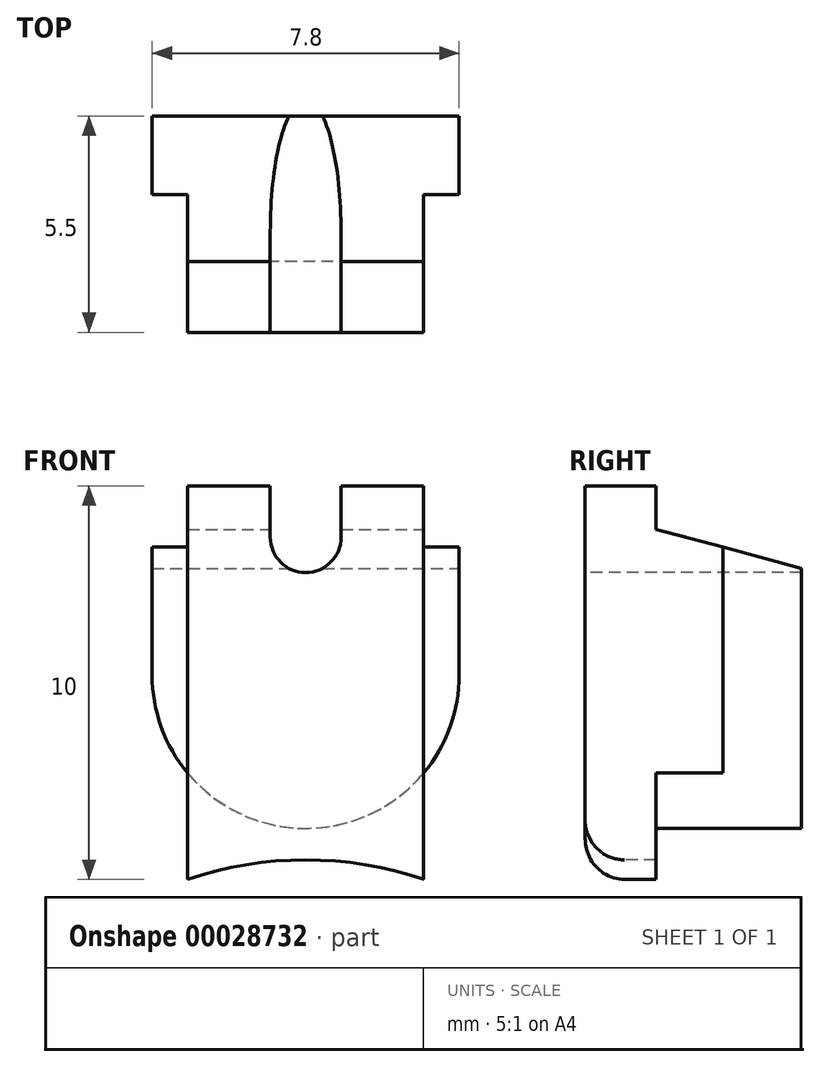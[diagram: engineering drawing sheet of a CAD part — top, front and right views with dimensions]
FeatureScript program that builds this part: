
annotation { "Feature Type Name" : "Feature", "Feature Type Description" : "" }
export const myFeature = defineFeature(function(context is Context, id is Id, definition is map)
    precondition{}
    {
        {
            var Q0;
            Q0=qCreatedBy(makeId("Front.planeOp"),FACE);
            var sketch = newSketch(context, id + "F0", { "sketchPlane" : qUnion([Q0])});
            skLineSegment(sketch, "E0", {"start": v(0, 8.83) * mm, "end": v(0, -12.43) * mm, "construction": true});
            skLineSegment(sketch, "E1.bottom", {"start": v(-3.9, 0) * mm, "end": v(0, 0) * mm});
            skLineSegment(sketch, "E1.top", {"start": v(-3.9, -10) * mm, "end": v(-3, -10) * mm});
            skLineSegment(sketch, "E1.left", {"start": v(-3.9, 0) * mm, "end": v(-3.9, -10) * mm});
            skLineSegment(sketch, "E1.right", {"start": v(3.9, 0) * mm, "end": v(3.9, -10) * mm});
            skLineSegment(sketch, "E2", {"start": v(-3, 0) * mm, "end": v(-3, -10) * mm});
            skLineSegment(sketch, "E3", {"start": v(3, 0) * mm, "end": v(3, -10) * mm});
            skLineSegment(sketch, "E4", {"start": v(-5.66, -9.5) * mm, "end": v(6.1, -9.5) * mm, "construction": true});
            skLineSegment(sketch, "E5", {"start": v(-5.46, -8.7) * mm, "end": v(6.54, -8.7) * mm, "construction": true});
            skLineSegment(sketch, "E6", {"start": v(-0.9, 0) * mm, "end": v(-0.9, -1.3) * mm});
            skArc(sketch, "E7", {"start": v(-0.9, -1.3) * mm, "mid": v(0, -2.2) * mm, "end": v(0.9, -1.3) * mm});
            skLineSegment(sketch, "E8", {"start": v(0.9, -1.3) * mm, "end": v(0.9, 0) * mm});
            skLineSegment(sketch, "E9.trimOffspring", {"start": v(0.9, 0) * mm, "end": v(3.9, 0) * mm});
            skArc(sketch, "E10", {"start": v(3, -10) * mm, "mid": v(0, -9.5) * mm, "end": v(-3, -10) * mm});
            skLineSegment(sketch, "E11.trimOffspring", {"start": v(3, -10) * mm, "end": v(3.9, -10) * mm});
            skArc(sketch, "E12", {"start": v(-3.9, -4.8) * mm, "mid": v(0, -8.7) * mm, "end": v(3.9, -4.8) * mm});
            skSolve(sketch);
        }
        {
            var Q0;
            Q0 = qSketchRegion(id + "F0", true);
            extrude(context, id + "F1", {"entities" : qUnion([Q0]), "oppositeDirection" : true, "depth" : 5.5 * mm});
        }
        {
            var Q0;
            Q0=makeQuery(id+"F1.opExtrude","SWEPT_FACE",FACE,{"disambiguationData":[OSD([sQuery(id+"F0.wireOp",EDGE,"E1.right")])]});
            var sketch = newSketch(context, id + "F2", { "sketchPlane" : qUnion([Q0])});
            skLineSegment(sketch, "E13", {"start": v(1.8, 0) * mm, "end": v(1.8, -1.1) * mm});
            skLineSegment(sketch, "E14", {"start": v(1.8, -1.1) * mm, "end": v(5.5, -2.1) * mm});
            skLineSegment(sketch, "E15", {"start": v(5.5, -2.1) * mm, "end": v(5.5, 0) * mm});
            skLineSegment(sketch, "E16", {"start": v(5.5, 0) * mm, "end": v(1.8, 0) * mm});
            skLineSegment(sketch, "E17", {"start": v(5.5, -8.7) * mm, "end": v(1.8, -8.7) * mm});
            skLineSegment(sketch, "E18", {"start": v(1.8, -8.7) * mm, "end": v(1.8, -10) * mm});
            skLineSegment(sketch, "E19", {"start": v(1.8, -10) * mm, "end": v(5.5, -10) * mm});
            skLineSegment(sketch, "E20", {"start": v(5.5, -10) * mm, "end": v(5.5, -8.7) * mm});
            skLineSegment(sketch, "E21", {"start": v(3.5, -1.56) * mm, "end": v(3.5, -8.7) * mm, "construction": true});
            skSolve(sketch);
        }
        {
            var Q0;
            Q0 = qSketchRegion(id + "F2", true);
            extrude(context, id + "F3", {"entities" : qUnion([Q0]), "operationType" : NewBodyOperationType.REMOVE, "endBound" : BoundingType.THROUGH_ALL, "oppositeDirection" : true, "depth" : 25 * mm});
        }
        {
            var Q0;
            Q0=sQuery(id+"F2.wireOp",VERTEX,"E21.end");
            var Q1;
            Q1=qCreatedBy(makeId("Front.planeOp"),FACE);
            cPlane(context, id + "F4", {"entities" : qUnion([Q0, Q1]), "cplaneType" : CPlaneType.PLANE_POINT, "offset" : 150 * mm, "width" : 150 * mm, "height" : 150 * mm});
        }
        {
            var Q0;
            Q0=qCreatedBy(id+"F4.planeOp",FACE);
            var sketch = newSketch(context, id + "F5", { "sketchPlane" : qUnion([Q0])});
            skLineSegment(sketch, "E22.0", {"start": v(3, 0) * mm, "end": v(3, -10) * mm});
            skLineSegment(sketch, "E22.1", {"start": v(-3, 0) * mm, "end": v(-3, -10) * mm});
            skLineSegment(sketch, "E23", {"start": v(3, 0) * mm, "end": v(3.9, 0) * mm});
            skLineSegment(sketch, "E24", {"start": v(3.9, 0) * mm, "end": v(3.9, -10) * mm});
            skLineSegment(sketch, "E25", {"start": v(3.9, -10) * mm, "end": v(3, -10) * mm});
            skLineSegment(sketch, "E26", {"start": v(-3, 0) * mm, "end": v(-3.9, 0) * mm});
            skLineSegment(sketch, "E27", {"start": v(-3.9, 0) * mm, "end": v(-3.9, -10) * mm});
            skLineSegment(sketch, "E28", {"start": v(-3.9, -10) * mm, "end": v(-3, -10) * mm});
            skSolve(sketch);
        }
        {
            var Q0;
            Q0 = qSketchRegion(id + "F5", true);
            extrude(context, id + "F6", {"entities" : qUnion([Q0]), "operationType" : NewBodyOperationType.REMOVE, "endBound" : BoundingType.THROUGH_ALL, "depth" : 25 * mm});
        }
        {
            var Q0;
            Q0=makeQuery(id+"F1.opExtrude","CAP_EDGE",EDGE,{"disambiguationData":[OSD([sQuery(id+"F0.wireOp",EDGE,"E10")])],"isStart":true});
            fillet(context, id + "F7", {"entities" : qUnion([Q0]), "radius" : 1 * mm, "tangentPropagation" : true, "allowEdgeOverflow" : false});
        }
        {
            var Q0;
            Q0=makeQuery(id+"F1.opExtrude","CAP_FACE",FACE,{"disambiguationData":[OSD([sQuery(id+"F0.wireOp",EDGE,"E1.bottom"),sQuery(id+"F0.wireOp",EDGE,"E1.top"),sQuery(id+"F0.wireOp",EDGE,"E1.left"),sQuery(id+"F0.wireOp",EDGE,"E1.right"),sQuery(id+"F0.wireOp",EDGE,"E6"),sQuery(id+"F0.wireOp",EDGE,"E7"),sQuery(id+"F0.wireOp",EDGE,"E8"),sQuery(id+"F0.wireOp",EDGE,"E9.trimOffspring"),sQuery(id+"F0.wireOp",EDGE,"E10"),sQuery(id+"F0.wireOp",EDGE,"E11.trimOffspring")])],"isStart":false});
            var sketch = newSketch(context, id + "F8", { "sketchPlane" : qUnion([Q0])});
            skArc(sketch, "E29.0", {"start": v(3.9, -4.8) * mm, "mid": v(0, -8.7) * mm, "end": v(-3.9, -4.8) * mm});
            skLineSegment(sketch, "E30", {"start": v(3.9, -4.8) * mm, "end": v(3.9, -8.7) * mm});
            skLineSegment(sketch, "E31", {"start": v(3.9, -8.7) * mm, "end": v(-3.9, -8.7) * mm});
            skLineSegment(sketch, "E32", {"start": v(-3.9, -8.7) * mm, "end": v(-3.9, -4.8) * mm});
            skSolve(sketch);
        }
        {
            var Q0;
            Q0 = qSketchRegion(id + "F8", true);
            var Q1;
            Q1=makeQuery(id+"F3.boolean.opBoolean","COPY",FACE,{"derivedFrom":makeQuery(id+"F3.opExtrude","SWEPT_FACE",FACE,{"disambiguationData":[OSD([sQuery(id+"F2.wireOp",EDGE,"E18")])]})});
            extrude(context, id + "F9", {"entities" : qUnion([Q0]), "operationType" : NewBodyOperationType.REMOVE, "endBound" : BoundingType.UP_TO_SURFACE, "oppositeDirection" : true, "endBoundEntityFace" : qUnion([Q1]), "depth" : 25 * mm});
        }
    });
